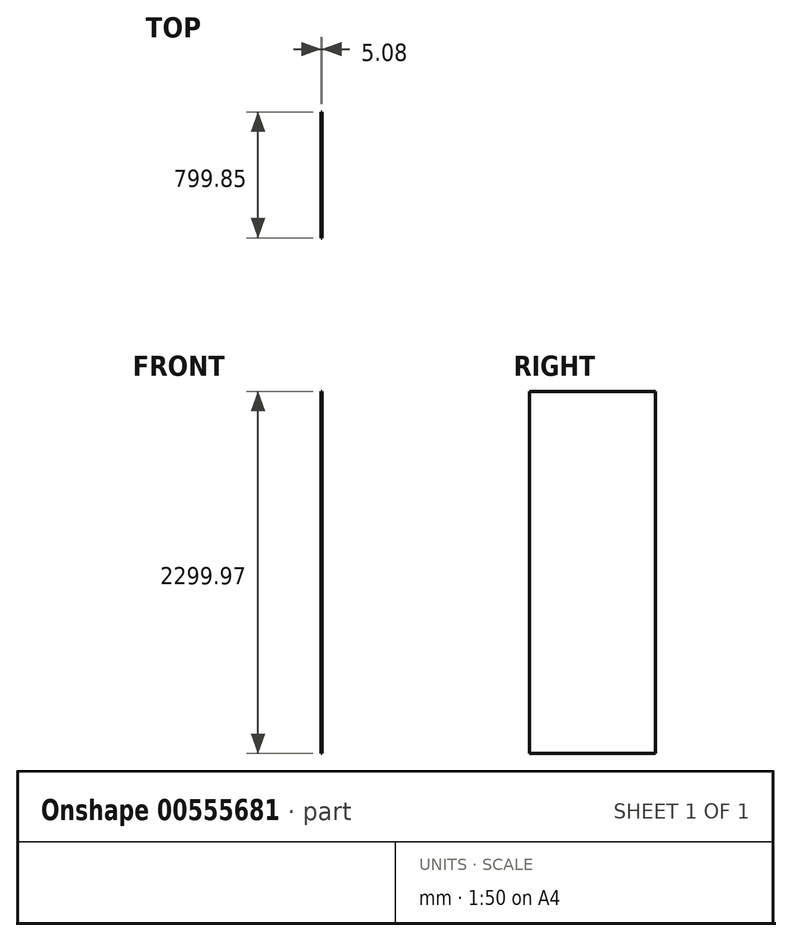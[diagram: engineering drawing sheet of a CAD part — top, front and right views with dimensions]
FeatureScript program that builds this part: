
annotation { "Feature Type Name" : "Feature", "Feature Type Description" : "" }
export const myFeature = defineFeature(function(context is Context, id is Id, definition is map)
    precondition{}
    {
        {
            var Q0;
            Q0=qCreatedBy(makeId("Front.planeOp"),FACE);
            var sketch = newSketch(context, id + "F0", { "sketchPlane" : qUnion([Q0])});
            skLineSegment(sketch, "E0.bottom", {"start": v(-83.27, 1154) * mm, "end": v(-78.2, 1154) * mm});
            skLineSegment(sketch, "E0.top", {"start": v(-83.27, -1145.97) * mm, "end": v(-78.2, -1145.97) * mm});
            skLineSegment(sketch, "E0.left", {"start": v(-83.27, 1154) * mm, "end": v(-83.27, -1145.97) * mm});
            skLineSegment(sketch, "E0.right", {"start": v(-78.2, 1154) * mm, "end": v(-78.2, -1145.97) * mm});
            skSolve(sketch);
        }
        {
            var Q0;
            Q0 = qSketchRegion(id + "F0", true);
            extrude(context, id + "F1", {"entities" : qUnion([Q0]), "depth" : 799.85 * mm, "offsetDistance" : 25.4 * mm});
        }
    });
